# Revit family: Column Caps (CC)-Side
name_source: partatom
category: Detail Items
revit_build: Autodesk Revit Architecture 2012 (Build: 20110210_1515)
units: mm (PartAtom-declared; Revit-internal decimal feet)

## types (17) — shared parameters
Finish = Gray Paint
Plate Thickness = 1/4"
Strap Width = 2 1/2"

## per-type parameters (varying)
| type | 4 Bolt Hole Vis | Height | Hole Diameter | Keynote | Length | Width End | Width Side | r |
| CC34-4 | Yes | 6 1/2" | 5/8" | 06 05 23.E31 | 11" | 3 1/4" | 3 5/8" | 5/16" |
| CC34-6 | Yes | 6 1/2" | 5/8" | 06 05 23.E32 | 11" | 3 1/4" | 5 1/2" | 5/16" |
| CC44 | No | 4" | 5/8" | 06 05 23.E33 | 7" | 3 5/8" | 3 5/8" | 5/16" |
| CC46 | No | 6 1/2" | 5/8" | 06 05 23.E34 | 11" | 3 5/8" | 5 1/2" | 5/16" |
| CC54-6 | No | 8" | 3/4" | 06 05 23.E35 | 13" | 5 1/4" | 5 1/2" | 3/8" |
| CC54-8 | No | 8" | 3/4" | 06 05 23.E36 | 13" | 5 1/4" | 7 1/2" | 3/8" |
| CC64 | No | 6 1/2" | 5/8" | 06 05 23.E37 | 11" | 5 1/2" | 3 5/8" | 5/16" |
| CC66 | No | 6 1/2" | 5/8" | 06 05 23.E38 | 11" | 5 1/2" | 5 1/2" | 5/16" |
| CC68 | No | 6 1/2" | 5/8" | 06 05 23.E39 | 11" | 5 1/2" | 7 1/2" | 5/16" |
| CC76 | No | 8" | 3/4" | 06 05 23.E40 | 13" | 6 7/8" | 5 1/2" | 3/8" |
| CC77 | No | 8" | 3/4" | 06 05 23.E41 | 13" | 6 7/8" | 6 7/8" | 3/8" |
| CC78 | No | 8" | 3/4" | 06 05 23.E42 | 13" | 6 7/8" | 7 1/2" | 3/8" |
| CC86 | No | 8" | 3/4" | 06 05 23.E43 | 13" | 7 1/2" | 5 1/2" | 3/8" |
| CC88 | No | 8" | 3/4" | 06 05 23.E44 | 13" | 7 1/2" | 7 1/2" | 3/8" |
| CC96 | No | 8" | 3/4" | 06 05 23.E45 | 13" | 8 7/8" | 5 1/2" | 3/8" |
| CC98 | No | 8" | 3/4" | 06 05 23.E46 | 13" | 8 7/8" | 7 1/2" | 3/8" |
| CC106 | No | 8" | 3/4" | 06 05 23.E47 | 13" | 9 1/2" | 5 1/2" | 3/8" |

## geometry (parser evidence)
native form markers: Sweep x1
no freeform markers — native parametric forms only
